# Revit family: Alcon-12100-10-R-Revit-Family
name_source: partatom
category: Lighting Fixtures
units: mm (PartAtom-declared; Revit-internal decimal feet)

## family parameters
Always vertical = Yes
Cut with Voids When Loaded = No
Host = Ceiling
Light Source = Yes
Part Type = Normal
Room Calculation Point = No
Round Connector Dimension = Use Diameter
Shared = No

## types (5) — shared parameters
Color Filter = 16777215
Default Elevation = 0' - 0"
Dimming Lamp Color Temperature Shift = <None>
Housing = Default
Led Source = Led Source
Lens = Lens
Light Source Symbol Size = 0' - 1"
Link To Product Page = https://www.alconlighting.com
Manufacturer = Alcon Light
Product Identity = Alcon Lighting 12100-10-R

## per-type parameters (varying)
| type | Emit from Line Length | Length |
| 12100-10-R-3' | 3' - 0" | 3' - 0" |
| 12100-10-R-4' | 4' - 0" | 4' - 0" |
| 12100-10-R-6' | 6' - 0" | 6' - 0" |
| 12100-10-R-2' | 2' - 0" | 2' - 0" |
| 12100-10-R-8' | 8' - 0" | 8' - 0" |

## geometry (parser evidence)
native form markers: Sweep x1
no freeform markers — native parametric forms only
